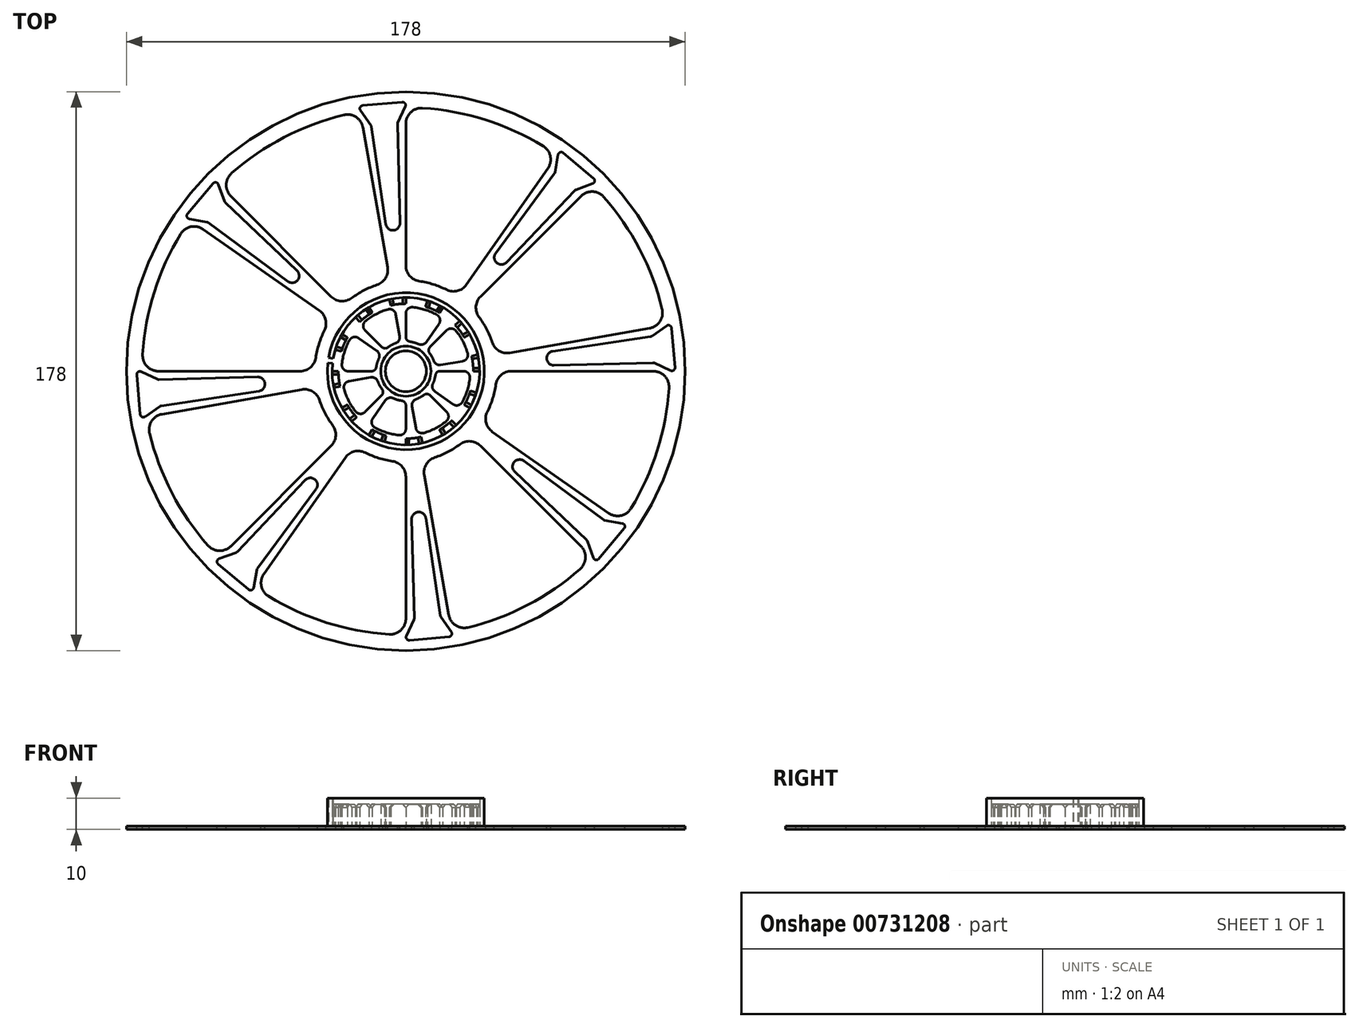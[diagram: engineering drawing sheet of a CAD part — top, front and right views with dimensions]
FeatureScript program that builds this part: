
annotation { "Feature Type Name" : "Feature", "Feature Type Description" : "" }
export const myFeature = defineFeature(function(context is Context, id is Id, definition is map)
    precondition{}
    {
        {
            var Q0;
            Q0=qCreatedBy(makeId("Top.planeOp"),FACE);
            var sketch = newSketch(context, id + "F0", { "sketchPlane" : qUnion([Q0])});
            skCircle(sketch, "E0", {"center": v(0, 0) * mm, "radius": 89 * mm});
            skCircle(sketch, "E1", {"center": v(0, 0) * mm, "radius": 6.5 * mm});
            skSolve(sketch);
        }
        {
            var Q0;
            Q0 = qSketchRegion(id + "F0", true);
            extrude(context, id + "F1", {"entities" : qUnion([Q0]), "depth" : 1 * mm, "offsetDistance" : 25 * mm});
        }
        {
            var Q0;
            Q0=makeQuery(id+"F1.opExtrude","CAP_FACE",FACE,{"disambiguationData":[OSD([sQuery(id+"F0.wireOp",EDGE,"E0"),sQuery(id+"F0.wireOp",EDGE,"E1")])],"isStart":false});
            var sketch = newSketch(context, id + "F2", { "sketchPlane" : qUnion([Q0])});
            skCircle(sketch, "E2", {"center": v(0, 0) * mm, "radius": 25 * mm});
            skCircle(sketch, "E3.0", {"center": v(0, 0) * mm, "radius": 23.5 * mm});
            skSolve(sketch);
        }
        {
            var Q0;
            Q0 = qSketchRegion(id + "F2", true);
            extrude(context, id + "F3", {"entities" : qUnion([Q0]), "operationType" : NewBodyOperationType.ADD, "depth" : 9 * mm, "offsetDistance" : 25 * mm});
        }
        {
            var Q0;
            {var subQ0=sQuery(id+"F0.wireOp",EDGE,"E0");Q0=makeQuery(id+"F3.boolean.opBoolean","SPLIT",FACE,{"disambiguationData":[TD([makeQuery(id+"F1.opExtrude","SWEPT_FACE",FACE,{"disambiguationData":[OSD([subQ0])]})])],"derivedFrom":makeQuery(id+"F1.opExtrude","CAP_FACE",FACE,{"disambiguationData":[OSD([subQ0,sQuery(id+"F0.wireOp",EDGE,"E1")])],"isStart":false})});}
            var sketch = newSketch(context, id + "F4", { "sketchPlane" : qUnion([Q0])});
            skLineSegment(sketch, "E4", {"start": v(-78.84, 0) * mm, "end": v(-33.63, 0) * mm});
            skLineSegment(sketch, "E5", {"start": v(-64.58, 45.22) * mm, "end": v(-27.55, 19.29) * mm});
            skPoint(sketch, "E6.center", {"position": v(0, 0) * mm});
            skArc(sketch, "E7", {"start": v(-28.68, 4.26) * mm, "mid": v(-27.66, 8.72) * mm, "end": v(-25.94, 12.96) * mm});
            skArc(sketch, "E8", {"start": v(-83.83, 5.32) * mm, "mid": v(-80.11, 25.26) * mm, "end": v(-71.72, 43.73) * mm});
            skPoint(sketch, "E9.visualSharp", {"position": v(-68.8, 48.18) * mm});
            skArc(sketch, "E9.filletArc", {"start": v(-64.58, 45.22) * mm, "mid": v(-68.47, 46.02) * mm, "end": v(-71.72, 43.73) * mm});
            skPoint(sketch, "E10.visualSharp", {"position": v(-84, 0) * mm});
            skArc(sketch, "E10.filletArc", {"start": v(-83.83, 5.32) * mm, "mid": v(-82.49, 1.58) * mm, "end": v(-78.84, 0) * mm});
            skPoint(sketch, "E11.visualSharp", {"position": v(-23.76, 16.63) * mm});
            skArc(sketch, "E11.filletArc", {"start": v(-25.94, 12.96) * mm, "mid": v(-25.57, 16.42) * mm, "end": v(-27.55, 19.29) * mm});
            skPoint(sketch, "E12.visualSharp", {"position": v(-29, 0) * mm});
            skArc(sketch, "E12.filletArc", {"start": v(-33.63, 0) * mm, "mid": v(-30.37, 1.21) * mm, "end": v(-28.68, 4.26) * mm});
            skArc(sketch, "E13.1.0", {"start": v(-63.04, -55.52) * mm, "mid": v(-74.5, -38.79) * mm, "end": v(-81.63, -19.8) * mm});
            skArc(sketch, "E13.1.1", {"start": v(-23.3, -17.27) * mm, "mid": v(-25.72, -13.4) * mm, "end": v(-27.5, -9.18) * mm});
            skPoint(sketch, "E13.1.2", {"position": v(-28.56, -5.04) * mm});
            skPoint(sketch, "E13.1.3", {"position": v(-59.4, -59.4) * mm});
            skPoint(sketch, "E13.1.4", {"position": v(-20.5, -20.5) * mm});
            skLineSegment(sketch, "E13.1.5", {"start": v(-77.64, -13.7) * mm, "end": v(-33.12, -5.84) * mm});
            skPoint(sketch, "E13.1.6", {"position": v(-82.72, -14.59) * mm});
            skLineSegment(sketch, "E13.1.7", {"start": v(-55.75, -55.75) * mm, "end": v(-23.78, -23.78) * mm});
            skArc(sketch, "E13.1.8", {"start": v(-63.04, -55.52) * mm, "mid": v(-59.44, -57.21) * mm, "end": v(-55.75, -55.75) * mm});
            skArc(sketch, "E13.1.9", {"start": v(-23.78, -23.78) * mm, "mid": v(-22.33, -20.61) * mm, "end": v(-23.3, -17.27) * mm});
            skArc(sketch, "E13.1.10", {"start": v(-27.5, -9.18) * mm, "mid": v(-29.7, -6.47) * mm, "end": v(-33.12, -5.84) * mm});
            skArc(sketch, "E13.1.11", {"start": v(-77.64, -13.7) * mm, "mid": v(-80.96, -15.88) * mm, "end": v(-81.63, -19.8) * mm});
            skArc(sketch, "E13.2.0", {"start": v(-5.32, -83.83) * mm, "mid": v(-25.26, -80.11) * mm, "end": v(-43.73, -71.72) * mm});
            skArc(sketch, "E13.2.1", {"start": v(-4.26, -28.68) * mm, "mid": v(-8.72, -27.66) * mm, "end": v(-12.96, -25.94) * mm});
            skPoint(sketch, "E13.2.2", {"position": v(-16.63, -23.76) * mm});
            skPoint(sketch, "E13.2.3", {"position": v(0, -84) * mm});
            skPoint(sketch, "E13.2.4", {"position": v(0, -29) * mm});
            skLineSegment(sketch, "E13.2.5", {"start": v(-45.22, -64.58) * mm, "end": v(-19.29, -27.55) * mm});
            skPoint(sketch, "E13.2.6", {"position": v(-48.18, -68.8) * mm});
            skLineSegment(sketch, "E13.2.7", {"start": v(0, -78.84) * mm, "end": v(0, -33.63) * mm});
            skArc(sketch, "E13.2.8", {"start": v(-5.32, -83.83) * mm, "mid": v(-1.58, -82.49) * mm, "end": v(0, -78.84) * mm});
            skArc(sketch, "E13.2.9", {"start": v(0, -33.63) * mm, "mid": v(-1.21, -30.37) * mm, "end": v(-4.26, -28.68) * mm});
            skArc(sketch, "E13.2.10", {"start": v(-12.96, -25.94) * mm, "mid": v(-16.42, -25.57) * mm, "end": v(-19.29, -27.55) * mm});
            skArc(sketch, "E13.2.11", {"start": v(-45.22, -64.58) * mm, "mid": v(-46.02, -68.47) * mm, "end": v(-43.73, -71.72) * mm});
            skArc(sketch, "E13.3.0", {"start": v(55.52, -63.04) * mm, "mid": v(38.79, -74.5) * mm, "end": v(19.8, -81.63) * mm});
            skArc(sketch, "E13.3.1", {"start": v(17.27, -23.3) * mm, "mid": v(13.4, -25.72) * mm, "end": v(9.18, -27.5) * mm});
            skPoint(sketch, "E13.3.2", {"position": v(5.04, -28.56) * mm});
            skPoint(sketch, "E13.3.3", {"position": v(59.4, -59.4) * mm});
            skPoint(sketch, "E13.3.4", {"position": v(20.5, -20.5) * mm});
            skLineSegment(sketch, "E13.3.5", {"start": v(13.7, -77.64) * mm, "end": v(5.84, -33.12) * mm});
            skPoint(sketch, "E13.3.6", {"position": v(14.59, -82.72) * mm});
            skLineSegment(sketch, "E13.3.7", {"start": v(55.75, -55.75) * mm, "end": v(23.78, -23.78) * mm});
            skArc(sketch, "E13.3.8", {"start": v(55.52, -63.04) * mm, "mid": v(57.21, -59.44) * mm, "end": v(55.75, -55.75) * mm});
            skArc(sketch, "E13.3.9", {"start": v(23.78, -23.78) * mm, "mid": v(20.61, -22.33) * mm, "end": v(17.27, -23.3) * mm});
            skArc(sketch, "E13.3.10", {"start": v(9.18, -27.5) * mm, "mid": v(6.47, -29.7) * mm, "end": v(5.84, -33.12) * mm});
            skArc(sketch, "E13.3.11", {"start": v(13.7, -77.64) * mm, "mid": v(15.88, -80.96) * mm, "end": v(19.8, -81.63) * mm});
            skArc(sketch, "E13.4.0", {"start": v(83.83, -5.32) * mm, "mid": v(80.11, -25.26) * mm, "end": v(71.72, -43.73) * mm});
            skArc(sketch, "E13.4.1", {"start": v(28.68, -4.26) * mm, "mid": v(27.66, -8.72) * mm, "end": v(25.94, -12.96) * mm});
            skPoint(sketch, "E13.4.2", {"position": v(23.76, -16.63) * mm});
            skPoint(sketch, "E13.4.3", {"position": v(84, 0) * mm});
            skPoint(sketch, "E13.4.4", {"position": v(29, 0) * mm});
            skLineSegment(sketch, "E13.4.5", {"start": v(64.58, -45.22) * mm, "end": v(27.55, -19.29) * mm});
            skPoint(sketch, "E13.4.6", {"position": v(68.8, -48.18) * mm});
            skLineSegment(sketch, "E13.4.7", {"start": v(78.84, 0) * mm, "end": v(33.63, 0) * mm});
            skArc(sketch, "E13.4.8", {"start": v(83.83, -5.32) * mm, "mid": v(82.49, -1.58) * mm, "end": v(78.84, 0) * mm});
            skArc(sketch, "E13.4.9", {"start": v(33.63, 0) * mm, "mid": v(30.37, -1.21) * mm, "end": v(28.68, -4.26) * mm});
            skArc(sketch, "E13.4.10", {"start": v(25.94, -12.96) * mm, "mid": v(25.57, -16.42) * mm, "end": v(27.55, -19.29) * mm});
            skArc(sketch, "E13.4.11", {"start": v(64.58, -45.22) * mm, "mid": v(68.47, -46.02) * mm, "end": v(71.72, -43.73) * mm});
            skArc(sketch, "E13.5.0", {"start": v(63.04, 55.52) * mm, "mid": v(74.5, 38.79) * mm, "end": v(81.63, 19.8) * mm});
            skArc(sketch, "E13.5.1", {"start": v(23.3, 17.27) * mm, "mid": v(25.72, 13.4) * mm, "end": v(27.5, 9.18) * mm});
            skPoint(sketch, "E13.5.2", {"position": v(28.56, 5.04) * mm});
            skPoint(sketch, "E13.5.3", {"position": v(59.4, 59.4) * mm});
            skPoint(sketch, "E13.5.4", {"position": v(20.5, 20.5) * mm});
            skLineSegment(sketch, "E13.5.5", {"start": v(77.64, 13.7) * mm, "end": v(33.12, 5.84) * mm});
            skPoint(sketch, "E13.5.6", {"position": v(82.72, 14.59) * mm});
            skLineSegment(sketch, "E13.5.7", {"start": v(55.75, 55.75) * mm, "end": v(23.78, 23.78) * mm});
            skArc(sketch, "E13.5.8", {"start": v(63.04, 55.52) * mm, "mid": v(59.44, 57.21) * mm, "end": v(55.75, 55.75) * mm});
            skArc(sketch, "E13.5.9", {"start": v(23.78, 23.78) * mm, "mid": v(22.33, 20.61) * mm, "end": v(23.3, 17.27) * mm});
            skArc(sketch, "E13.5.10", {"start": v(27.5, 9.18) * mm, "mid": v(29.7, 6.47) * mm, "end": v(33.12, 5.84) * mm});
            skArc(sketch, "E13.5.11", {"start": v(77.64, 13.7) * mm, "mid": v(80.96, 15.88) * mm, "end": v(81.63, 19.8) * mm});
            skArc(sketch, "E13.6.0", {"start": v(5.32, 83.83) * mm, "mid": v(25.26, 80.11) * mm, "end": v(43.73, 71.72) * mm});
            skArc(sketch, "E13.6.1", {"start": v(4.26, 28.68) * mm, "mid": v(8.72, 27.66) * mm, "end": v(12.96, 25.94) * mm});
            skPoint(sketch, "E13.6.2", {"position": v(16.63, 23.76) * mm});
            skPoint(sketch, "E13.6.3", {"position": v(0, 84) * mm});
            skPoint(sketch, "E13.6.4", {"position": v(0, 29) * mm});
            skLineSegment(sketch, "E13.6.5", {"start": v(45.22, 64.58) * mm, "end": v(19.29, 27.55) * mm});
            skPoint(sketch, "E13.6.6", {"position": v(48.18, 68.8) * mm});
            skLineSegment(sketch, "E13.6.7", {"start": v(0, 78.84) * mm, "end": v(0, 33.63) * mm});
            skArc(sketch, "E13.6.8", {"start": v(5.32, 83.83) * mm, "mid": v(1.58, 82.49) * mm, "end": v(0, 78.84) * mm});
            skArc(sketch, "E13.6.9", {"start": v(0, 33.63) * mm, "mid": v(1.21, 30.37) * mm, "end": v(4.26, 28.68) * mm});
            skArc(sketch, "E13.6.10", {"start": v(12.96, 25.94) * mm, "mid": v(16.42, 25.57) * mm, "end": v(19.29, 27.55) * mm});
            skArc(sketch, "E13.6.11", {"start": v(45.22, 64.58) * mm, "mid": v(46.02, 68.47) * mm, "end": v(43.73, 71.72) * mm});
            skArc(sketch, "E13.7.0", {"start": v(-55.52, 63.04) * mm, "mid": v(-38.79, 74.5) * mm, "end": v(-19.8, 81.63) * mm});
            skArc(sketch, "E13.7.1", {"start": v(-17.27, 23.3) * mm, "mid": v(-13.4, 25.72) * mm, "end": v(-9.18, 27.5) * mm});
            skPoint(sketch, "E13.7.2", {"position": v(-5.04, 28.56) * mm});
            skPoint(sketch, "E13.7.3", {"position": v(-59.4, 59.4) * mm});
            skPoint(sketch, "E13.7.4", {"position": v(-20.5, 20.5) * mm});
            skLineSegment(sketch, "E13.7.5", {"start": v(-13.7, 77.64) * mm, "end": v(-5.84, 33.12) * mm});
            skPoint(sketch, "E13.7.6", {"position": v(-14.59, 82.72) * mm});
            skLineSegment(sketch, "E13.7.7", {"start": v(-55.75, 55.75) * mm, "end": v(-23.78, 23.78) * mm});
            skArc(sketch, "E13.7.8", {"start": v(-55.52, 63.04) * mm, "mid": v(-57.21, 59.44) * mm, "end": v(-55.75, 55.75) * mm});
            skArc(sketch, "E13.7.9", {"start": v(-23.78, 23.78) * mm, "mid": v(-20.61, 22.33) * mm, "end": v(-17.27, 23.3) * mm});
            skArc(sketch, "E13.7.10", {"start": v(-9.18, 27.5) * mm, "mid": v(-6.47, 29.7) * mm, "end": v(-5.84, 33.12) * mm});
            skArc(sketch, "E13.7.11", {"start": v(-13.7, 77.64) * mm, "mid": v(-15.88, 80.96) * mm, "end": v(-19.8, 81.63) * mm});
            skLineSegment(sketch, "E14", {"start": v(-62.9, 47.32) * mm, "end": v(-37.6, 28.6) * mm});
            skLineSegment(sketch, "E15", {"start": v(-34.7, 32.07) * mm, "end": v(-57.52, 53.73) * mm});
            skLineSegment(sketch, "E16", {"start": v(-57.78, 54.12) * mm, "end": v(-59.73, 59.5) * mm});
            skLineSegment(sketch, "E17", {"start": v(-68.96, 48.5) * mm, "end": v(-63.33, 47.5) * mm});
            skArc(sketch, "E18", {"start": v(-37.6, 28.6) * mm, "mid": v(-34.52, 28.96) * mm, "end": v(-34.7, 32.07) * mm});
            skLineSegment(sketch, "E19", {"start": v(-57.7, 53.9) * mm, "end": v(-63.1, 47.46) * mm, "construction": true});
            skPoint(sketch, "E20", {"position": v(-60.4, 50.68) * mm});
            skLineSegment(sketch, "E21", {"start": v(-60.4, 50.68) * mm, "end": v(-36.25, 30.42) * mm, "construction": true});
            skLineSegment(sketch, "E22", {"start": v(-61.44, 59.8) * mm, "end": v(-69.56, 50.12) * mm});
            skPoint(sketch, "E23", {"position": v(-65.5, 54.96) * mm});
            skPoint(sketch, "E24", {"position": v(-68.18, 57.2) * mm});
            skLineSegment(sketch, "E25", {"start": v(-57.27, 70.2) * mm, "end": v(-81.87, 40.9) * mm, "construction": true});
            skPoint(sketch, "E26.visualSharp", {"position": v(-70.67, 48.8) * mm});
            skArc(sketch, "E26.filletArc", {"start": v(-69.56, 50.12) * mm, "mid": v(-69.73, 49.14) * mm, "end": v(-68.96, 48.5) * mm});
            skPoint(sketch, "E27.visualSharp", {"position": v(-60.33, 61.12) * mm});
            skArc(sketch, "E27.filletArc", {"start": v(-59.73, 59.5) * mm, "mid": v(-60.5, 60.14) * mm, "end": v(-61.44, 59.8) * mm});
            skPoint(sketch, "E28.visualSharp", {"position": v(-57.7, 53.9) * mm});
            skArc(sketch, "E28.filletArc", {"start": v(-57.78, 54.12) * mm, "mid": v(-57.67, 53.91) * mm, "end": v(-57.52, 53.73) * mm});
            skPoint(sketch, "E29.visualSharp", {"position": v(-63.1, 47.46) * mm});
            skArc(sketch, "E29.filletArc", {"start": v(-62.9, 47.32) * mm, "mid": v(-63.1, 47.43) * mm, "end": v(-63.33, 47.5) * mm});
            skArc(sketch, "E30", {"start": v(-64.58, 45.22) * mm, "mid": v(-62.55, 48) * mm, "end": v(-60.4, 50.68) * mm, "construction": true});
            skArc(sketch, "E31.1.0", {"start": v(-46.81, -6.37) * mm, "mid": v(-44.88, -3.93) * mm, "end": v(-47.2, -1.86) * mm});
            skLineSegment(sketch, "E31.1.1", {"start": v(-77.94, -11.02) * mm, "end": v(-46.81, -6.37) * mm});
            skLineSegment(sketch, "E31.1.2", {"start": v(-47.2, -1.86) * mm, "end": v(-78.67, -2.68) * mm});
            skLineSegment(sketch, "E31.1.3", {"start": v(-79.12, -2.59) * mm, "end": v(-84.3, -0.17) * mm});
            skLineSegment(sketch, "E31.1.4", {"start": v(-85.72, -1.16) * mm, "end": v(-84.62, -13.74) * mm});
            skLineSegment(sketch, "E31.1.5", {"start": v(-83.05, -14.47) * mm, "end": v(-78.37, -11.2) * mm});
            skArc(sketch, "E31.1.6", {"start": v(-84.62, -13.74) * mm, "mid": v(-84.05, -14.56) * mm, "end": v(-83.05, -14.47) * mm});
            skArc(sketch, "E31.1.7", {"start": v(-84.3, -0.17) * mm, "mid": v(-85.3, -0.26) * mm, "end": v(-85.72, -1.16) * mm});
            skArc(sketch, "E31.1.8", {"start": v(-79.12, -2.59) * mm, "mid": v(-78.9, -2.66) * mm, "end": v(-78.67, -2.68) * mm});
            skArc(sketch, "E31.1.9", {"start": v(-77.94, -11.02) * mm, "mid": v(-78.17, -11.08) * mm, "end": v(-78.37, -11.2) * mm});
            skArc(sketch, "E31.2.0", {"start": v(-28.6, -37.6) * mm, "mid": v(-28.96, -34.52) * mm, "end": v(-32.07, -34.7) * mm});
            skLineSegment(sketch, "E31.2.1", {"start": v(-47.32, -62.9) * mm, "end": v(-28.6, -37.6) * mm});
            skLineSegment(sketch, "E31.2.2", {"start": v(-32.07, -34.7) * mm, "end": v(-53.73, -57.52) * mm});
            skLineSegment(sketch, "E31.2.3", {"start": v(-54.12, -57.78) * mm, "end": v(-59.5, -59.73) * mm});
            skLineSegment(sketch, "E31.2.4", {"start": v(-59.8, -61.44) * mm, "end": v(-50.12, -69.56) * mm});
            skLineSegment(sketch, "E31.2.5", {"start": v(-48.5, -68.96) * mm, "end": v(-47.5, -63.33) * mm});
            skArc(sketch, "E31.2.6", {"start": v(-50.12, -69.56) * mm, "mid": v(-49.14, -69.73) * mm, "end": v(-48.5, -68.96) * mm});
            skArc(sketch, "E31.2.7", {"start": v(-59.5, -59.73) * mm, "mid": v(-60.14, -60.5) * mm, "end": v(-59.8, -61.44) * mm});
            skArc(sketch, "E31.2.8", {"start": v(-54.12, -57.78) * mm, "mid": v(-53.91, -57.67) * mm, "end": v(-53.73, -57.52) * mm});
            skArc(sketch, "E31.2.9", {"start": v(-47.32, -62.9) * mm, "mid": v(-47.43, -63.1) * mm, "end": v(-47.5, -63.33) * mm});
            skArc(sketch, "E31.3.0", {"start": v(6.37, -46.81) * mm, "mid": v(3.93, -44.88) * mm, "end": v(1.86, -47.2) * mm});
            skLineSegment(sketch, "E31.3.1", {"start": v(11.02, -77.94) * mm, "end": v(6.37, -46.81) * mm});
            skLineSegment(sketch, "E31.3.2", {"start": v(1.86, -47.2) * mm, "end": v(2.68, -78.67) * mm});
            skLineSegment(sketch, "E31.3.3", {"start": v(2.59, -79.12) * mm, "end": v(0.17, -84.3) * mm});
            skLineSegment(sketch, "E31.3.4", {"start": v(1.16, -85.72) * mm, "end": v(13.74, -84.62) * mm});
            skLineSegment(sketch, "E31.3.5", {"start": v(14.47, -83.05) * mm, "end": v(11.2, -78.37) * mm});
            skArc(sketch, "E31.3.6", {"start": v(13.74, -84.62) * mm, "mid": v(14.56, -84.05) * mm, "end": v(14.47, -83.05) * mm});
            skArc(sketch, "E31.3.7", {"start": v(0.17, -84.3) * mm, "mid": v(0.26, -85.3) * mm, "end": v(1.16, -85.72) * mm});
            skArc(sketch, "E31.3.8", {"start": v(2.59, -79.12) * mm, "mid": v(2.66, -78.9) * mm, "end": v(2.68, -78.67) * mm});
            skArc(sketch, "E31.3.9", {"start": v(11.02, -77.94) * mm, "mid": v(11.08, -78.17) * mm, "end": v(11.2, -78.37) * mm});
            skArc(sketch, "E31.4.0", {"start": v(37.6, -28.6) * mm, "mid": v(34.52, -28.96) * mm, "end": v(34.7, -32.07) * mm});
            skLineSegment(sketch, "E31.4.1", {"start": v(62.9, -47.32) * mm, "end": v(37.6, -28.6) * mm});
            skLineSegment(sketch, "E31.4.2", {"start": v(34.7, -32.07) * mm, "end": v(57.52, -53.73) * mm});
            skLineSegment(sketch, "E31.4.3", {"start": v(57.78, -54.12) * mm, "end": v(59.73, -59.5) * mm});
            skLineSegment(sketch, "E31.4.4", {"start": v(61.44, -59.8) * mm, "end": v(69.56, -50.12) * mm});
            skLineSegment(sketch, "E31.4.5", {"start": v(68.96, -48.5) * mm, "end": v(63.33, -47.5) * mm});
            skArc(sketch, "E31.4.6", {"start": v(69.56, -50.12) * mm, "mid": v(69.73, -49.14) * mm, "end": v(68.96, -48.5) * mm});
            skArc(sketch, "E31.4.7", {"start": v(59.73, -59.5) * mm, "mid": v(60.5, -60.14) * mm, "end": v(61.44, -59.8) * mm});
            skArc(sketch, "E31.4.8", {"start": v(57.78, -54.12) * mm, "mid": v(57.67, -53.91) * mm, "end": v(57.52, -53.73) * mm});
            skArc(sketch, "E31.4.9", {"start": v(62.9, -47.32) * mm, "mid": v(63.1, -47.43) * mm, "end": v(63.33, -47.5) * mm});
            skArc(sketch, "E31.5.0", {"start": v(46.81, 6.37) * mm, "mid": v(44.88, 3.93) * mm, "end": v(47.2, 1.86) * mm});
            skLineSegment(sketch, "E31.5.1", {"start": v(77.94, 11.02) * mm, "end": v(46.81, 6.37) * mm});
            skLineSegment(sketch, "E31.5.2", {"start": v(47.2, 1.86) * mm, "end": v(78.67, 2.68) * mm});
            skLineSegment(sketch, "E31.5.3", {"start": v(79.12, 2.59) * mm, "end": v(84.3, 0.17) * mm});
            skLineSegment(sketch, "E31.5.4", {"start": v(85.72, 1.16) * mm, "end": v(84.62, 13.74) * mm});
            skLineSegment(sketch, "E31.5.5", {"start": v(83.05, 14.47) * mm, "end": v(78.37, 11.2) * mm});
            skArc(sketch, "E31.5.6", {"start": v(84.62, 13.74) * mm, "mid": v(84.05, 14.56) * mm, "end": v(83.05, 14.47) * mm});
            skArc(sketch, "E31.5.7", {"start": v(84.3, 0.17) * mm, "mid": v(85.3, 0.26) * mm, "end": v(85.72, 1.16) * mm});
            skArc(sketch, "E31.5.8", {"start": v(79.12, 2.59) * mm, "mid": v(78.9, 2.66) * mm, "end": v(78.67, 2.68) * mm});
            skArc(sketch, "E31.5.9", {"start": v(77.94, 11.02) * mm, "mid": v(78.17, 11.08) * mm, "end": v(78.37, 11.2) * mm});
            skArc(sketch, "E31.6.0", {"start": v(28.6, 37.6) * mm, "mid": v(28.96, 34.52) * mm, "end": v(32.07, 34.7) * mm});
            skLineSegment(sketch, "E31.6.1", {"start": v(47.32, 62.9) * mm, "end": v(28.6, 37.6) * mm});
            skLineSegment(sketch, "E31.6.2", {"start": v(32.07, 34.7) * mm, "end": v(53.73, 57.52) * mm});
            skLineSegment(sketch, "E31.6.3", {"start": v(54.12, 57.78) * mm, "end": v(59.5, 59.73) * mm});
            skLineSegment(sketch, "E31.6.4", {"start": v(59.8, 61.44) * mm, "end": v(50.12, 69.56) * mm});
            skLineSegment(sketch, "E31.6.5", {"start": v(48.5, 68.96) * mm, "end": v(47.5, 63.33) * mm});
            skArc(sketch, "E31.6.6", {"start": v(50.12, 69.56) * mm, "mid": v(49.14, 69.73) * mm, "end": v(48.5, 68.96) * mm});
            skArc(sketch, "E31.6.7", {"start": v(59.5, 59.73) * mm, "mid": v(60.14, 60.5) * mm, "end": v(59.8, 61.44) * mm});
            skArc(sketch, "E31.6.8", {"start": v(54.12, 57.78) * mm, "mid": v(53.91, 57.67) * mm, "end": v(53.73, 57.52) * mm});
            skArc(sketch, "E31.6.9", {"start": v(47.32, 62.9) * mm, "mid": v(47.43, 63.1) * mm, "end": v(47.5, 63.33) * mm});
            skArc(sketch, "E31.7.0", {"start": v(-6.37, 46.81) * mm, "mid": v(-3.93, 44.88) * mm, "end": v(-1.86, 47.2) * mm});
            skLineSegment(sketch, "E31.7.1", {"start": v(-11.02, 77.94) * mm, "end": v(-6.37, 46.81) * mm});
            skLineSegment(sketch, "E31.7.2", {"start": v(-1.86, 47.2) * mm, "end": v(-2.68, 78.67) * mm});
            skLineSegment(sketch, "E31.7.3", {"start": v(-2.59, 79.12) * mm, "end": v(-0.17, 84.3) * mm});
            skLineSegment(sketch, "E31.7.4", {"start": v(-1.16, 85.72) * mm, "end": v(-13.74, 84.62) * mm});
            skLineSegment(sketch, "E31.7.5", {"start": v(-14.47, 83.05) * mm, "end": v(-11.2, 78.37) * mm});
            skArc(sketch, "E31.7.6", {"start": v(-13.74, 84.62) * mm, "mid": v(-14.56, 84.05) * mm, "end": v(-14.47, 83.05) * mm});
            skArc(sketch, "E31.7.7", {"start": v(-0.17, 84.3) * mm, "mid": v(-0.26, 85.3) * mm, "end": v(-1.16, 85.72) * mm});
            skArc(sketch, "E31.7.8", {"start": v(-2.59, 79.12) * mm, "mid": v(-2.66, 78.9) * mm, "end": v(-2.68, 78.67) * mm});
            skArc(sketch, "E31.7.9", {"start": v(-11.02, 77.94) * mm, "mid": v(-11.08, 78.17) * mm, "end": v(-11.2, 78.37) * mm});
            skLineSegment(sketch, "E32", {"start": v(-18.4, 0) * mm, "end": v(-10.9, 0) * mm});
            skLineSegment(sketch, "E33", {"start": v(-9.28, 6.5) * mm, "end": v(-15.07, 10.55) * mm});
            skArc(sketch, "E34", {"start": v(-9.41, 1.3) * mm, "mid": v(-9.11, 2.68) * mm, "end": v(-8.61, 4.01) * mm});
            skArc(sketch, "E35", {"start": v(-20.38, 2.22) * mm, "mid": v(-19.55, 6.16) * mm, "end": v(-17.97, 9.87) * mm});
            skPoint(sketch, "E36.visualSharp", {"position": v(-16.8, 11.76) * mm});
            skArc(sketch, "E36.filletArc", {"start": v(-15.07, 10.55) * mm, "mid": v(-16.67, 10.86) * mm, "end": v(-17.97, 9.87) * mm});
            skPoint(sketch, "E37.visualSharp", {"position": v(-20.5, 0) * mm});
            skArc(sketch, "E37.filletArc", {"start": v(-20.38, 2.22) * mm, "mid": v(-19.88, 0.66) * mm, "end": v(-18.4, 0) * mm});
            skPoint(sketch, "E38.visualSharp", {"position": v(-9.5, 0) * mm});
            skArc(sketch, "E38.filletArc", {"start": v(-10.9, 0) * mm, "mid": v(-9.91, 0.37) * mm, "end": v(-9.41, 1.3) * mm});
            skPoint(sketch, "E39.visualSharp", {"position": v(-7.78, 5.45) * mm});
            skArc(sketch, "E39.filletArc", {"start": v(-8.61, 4.01) * mm, "mid": v(-8.5, 5.38) * mm, "end": v(-9.28, 6.5) * mm});
            skLineSegment(sketch, "E40.1.0", {"start": v(-13, -13) * mm, "end": v(-7.7, -7.7) * mm});
            skArc(sketch, "E40.1.1", {"start": v(-7.57, -5.74) * mm, "mid": v(-8.34, -4.55) * mm, "end": v(-8.93, -3.25) * mm});
            skPoint(sketch, "E40.1.2", {"position": v(-20.19, -3.56) * mm});
            skPoint(sketch, "E40.1.3", {"position": v(-9.36, -1.65) * mm});
            skPoint(sketch, "E40.1.4", {"position": v(-6.72, -6.72) * mm});
            skLineSegment(sketch, "E40.1.5", {"start": v(-11.15, -1.97) * mm, "end": v(-18.11, -3.2) * mm});
            skArc(sketch, "E40.1.6", {"start": v(-8.93, -3.25) * mm, "mid": v(-9.8, -2.2) * mm, "end": v(-11.15, -1.97) * mm});
            skArc(sketch, "E40.1.7", {"start": v(-18.11, -3.2) * mm, "mid": v(-19.46, -4.1) * mm, "end": v(-19.69, -5.72) * mm});
            skArc(sketch, "E40.1.8", {"start": v(-7.7, -7.7) * mm, "mid": v(-7.27, -6.75) * mm, "end": v(-7.57, -5.74) * mm});
            skArc(sketch, "E40.1.9", {"start": v(-15.98, -12.84) * mm, "mid": v(-14.53, -13.59) * mm, "end": v(-13, -13) * mm});
            skArc(sketch, "E40.1.10", {"start": v(-15.98, -12.84) * mm, "mid": v(-18.18, -9.47) * mm, "end": v(-19.69, -5.72) * mm});
            skLineSegment(sketch, "E40.2.0", {"start": v(0, -18.4) * mm, "end": v(0, -10.9) * mm});
            skArc(sketch, "E40.2.1", {"start": v(-1.3, -9.41) * mm, "mid": v(-2.68, -9.11) * mm, "end": v(-4.01, -8.61) * mm});
            skPoint(sketch, "E40.2.2", {"position": v(-11.76, -16.8) * mm});
            skPoint(sketch, "E40.2.3", {"position": v(-5.45, -7.78) * mm});
            skPoint(sketch, "E40.2.4", {"position": v(0, -9.5) * mm});
            skLineSegment(sketch, "E40.2.5", {"start": v(-6.5, -9.28) * mm, "end": v(-10.55, -15.07) * mm});
            skArc(sketch, "E40.2.6", {"start": v(-4.01, -8.61) * mm, "mid": v(-5.38, -8.5) * mm, "end": v(-6.5, -9.28) * mm});
            skArc(sketch, "E40.2.7", {"start": v(-10.55, -15.07) * mm, "mid": v(-10.86, -16.67) * mm, "end": v(-9.87, -17.97) * mm});
            skArc(sketch, "E40.2.8", {"start": v(0, -10.9) * mm, "mid": v(-0.37, -9.91) * mm, "end": v(-1.3, -9.41) * mm});
            skArc(sketch, "E40.2.9", {"start": v(-2.22, -20.38) * mm, "mid": v(-0.66, -19.88) * mm, "end": v(0, -18.4) * mm});
            skArc(sketch, "E40.2.10", {"start": v(-2.22, -20.38) * mm, "mid": v(-6.16, -19.55) * mm, "end": v(-9.87, -17.97) * mm});
            skLineSegment(sketch, "E40.3.0", {"start": v(13, -13) * mm, "end": v(7.7, -7.7) * mm});
            skArc(sketch, "E40.3.1", {"start": v(5.74, -7.57) * mm, "mid": v(4.55, -8.34) * mm, "end": v(3.25, -8.93) * mm});
            skPoint(sketch, "E40.3.2", {"position": v(3.56, -20.19) * mm});
            skPoint(sketch, "E40.3.3", {"position": v(1.65, -9.36) * mm});
            skPoint(sketch, "E40.3.4", {"position": v(6.72, -6.72) * mm});
            skLineSegment(sketch, "E40.3.5", {"start": v(1.97, -11.15) * mm, "end": v(3.2, -18.11) * mm});
            skArc(sketch, "E40.3.6", {"start": v(3.25, -8.93) * mm, "mid": v(2.2, -9.8) * mm, "end": v(1.97, -11.15) * mm});
            skArc(sketch, "E40.3.7", {"start": v(3.2, -18.11) * mm, "mid": v(4.1, -19.46) * mm, "end": v(5.72, -19.69) * mm});
            skArc(sketch, "E40.3.8", {"start": v(7.7, -7.7) * mm, "mid": v(6.75, -7.27) * mm, "end": v(5.74, -7.57) * mm});
            skArc(sketch, "E40.3.9", {"start": v(12.84, -15.98) * mm, "mid": v(13.59, -14.53) * mm, "end": v(13, -13) * mm});
            skArc(sketch, "E40.3.10", {"start": v(12.84, -15.98) * mm, "mid": v(9.47, -18.18) * mm, "end": v(5.72, -19.69) * mm});
            skLineSegment(sketch, "E40.4.0", {"start": v(18.4, 0) * mm, "end": v(10.9, 0) * mm});
            skArc(sketch, "E40.4.1", {"start": v(9.41, -1.3) * mm, "mid": v(9.11, -2.68) * mm, "end": v(8.61, -4.01) * mm});
            skPoint(sketch, "E40.4.2", {"position": v(16.8, -11.76) * mm});
            skPoint(sketch, "E40.4.3", {"position": v(7.78, -5.45) * mm});
            skPoint(sketch, "E40.4.4", {"position": v(9.5, 0) * mm});
            skLineSegment(sketch, "E40.4.5", {"start": v(9.28, -6.5) * mm, "end": v(15.07, -10.55) * mm});
            skArc(sketch, "E40.4.6", {"start": v(8.61, -4.01) * mm, "mid": v(8.5, -5.38) * mm, "end": v(9.28, -6.5) * mm});
            skArc(sketch, "E40.4.7", {"start": v(15.07, -10.55) * mm, "mid": v(16.67, -10.86) * mm, "end": v(17.97, -9.87) * mm});
            skArc(sketch, "E40.4.8", {"start": v(10.9, 0) * mm, "mid": v(9.91, -0.37) * mm, "end": v(9.41, -1.3) * mm});
            skArc(sketch, "E40.4.9", {"start": v(20.38, -2.22) * mm, "mid": v(19.88, -0.66) * mm, "end": v(18.4, 0) * mm});
            skArc(sketch, "E40.4.10", {"start": v(20.38, -2.22) * mm, "mid": v(19.55, -6.16) * mm, "end": v(17.97, -9.87) * mm});
            skLineSegment(sketch, "E40.5.0", {"start": v(13, 13) * mm, "end": v(7.7, 7.7) * mm});
            skArc(sketch, "E40.5.1", {"start": v(7.57, 5.74) * mm, "mid": v(8.34, 4.55) * mm, "end": v(8.93, 3.25) * mm});
            skPoint(sketch, "E40.5.2", {"position": v(20.19, 3.56) * mm});
            skPoint(sketch, "E40.5.3", {"position": v(9.36, 1.65) * mm});
            skPoint(sketch, "E40.5.4", {"position": v(6.72, 6.72) * mm});
            skLineSegment(sketch, "E40.5.5", {"start": v(11.15, 1.97) * mm, "end": v(18.11, 3.2) * mm});
            skArc(sketch, "E40.5.6", {"start": v(8.93, 3.25) * mm, "mid": v(9.8, 2.2) * mm, "end": v(11.15, 1.97) * mm});
            skArc(sketch, "E40.5.7", {"start": v(18.11, 3.2) * mm, "mid": v(19.46, 4.1) * mm, "end": v(19.69, 5.72) * mm});
            skArc(sketch, "E40.5.8", {"start": v(7.7, 7.7) * mm, "mid": v(7.27, 6.75) * mm, "end": v(7.57, 5.74) * mm});
            skArc(sketch, "E40.5.9", {"start": v(15.98, 12.84) * mm, "mid": v(14.53, 13.59) * mm, "end": v(13, 13) * mm});
            skArc(sketch, "E40.5.10", {"start": v(15.98, 12.84) * mm, "mid": v(18.18, 9.47) * mm, "end": v(19.69, 5.72) * mm});
            skLineSegment(sketch, "E41.1.6.0", {"start": v(0, 18.4) * mm, "end": v(0, 10.9) * mm});
            skArc(sketch, "E41.3.6.0", {"start": v(1.3, 9.41) * mm, "mid": v(2.68, 9.11) * mm, "end": v(4.01, 8.61) * mm});
            skPoint(sketch, "E41.7.6.0", {"position": v(11.76, 16.8) * mm});
            skPoint(sketch, "E41.8.6.0", {"position": v(5.45, 7.78) * mm});
            skPoint(sketch, "E41.9.6.0", {"position": v(0, 9.5) * mm});
            skLineSegment(sketch, "E41.10.6.0", {"start": v(6.5, 9.28) * mm, "end": v(10.55, 15.07) * mm});
            skArc(sketch, "E41.13.6.0", {"start": v(4.01, 8.61) * mm, "mid": v(5.38, 8.5) * mm, "end": v(6.5, 9.28) * mm});
            skArc(sketch, "E41.17.6.0", {"start": v(10.55, 15.07) * mm, "mid": v(10.86, 16.67) * mm, "end": v(9.87, 17.97) * mm});
            skArc(sketch, "E41.21.6.0", {"start": v(0, 10.9) * mm, "mid": v(0.37, 9.91) * mm, "end": v(1.3, 9.41) * mm});
            skArc(sketch, "E41.25.6.0", {"start": v(2.22, 20.38) * mm, "mid": v(0.66, 19.88) * mm, "end": v(0, 18.4) * mm});
            skArc(sketch, "E41.29.6.0", {"start": v(2.22, 20.38) * mm, "mid": v(6.16, 19.55) * mm, "end": v(9.87, 17.97) * mm});
            skLineSegment(sketch, "E41.1.7.0", {"start": v(-13, 13) * mm, "end": v(-7.7, 7.7) * mm});
            skArc(sketch, "E41.3.7.0", {"start": v(-5.74, 7.57) * mm, "mid": v(-4.55, 8.34) * mm, "end": v(-3.25, 8.93) * mm});
            skPoint(sketch, "E41.7.7.0", {"position": v(-3.56, 20.19) * mm});
            skPoint(sketch, "E41.8.7.0", {"position": v(-1.65, 9.36) * mm});
            skPoint(sketch, "E41.9.7.0", {"position": v(-6.72, 6.72) * mm});
            skLineSegment(sketch, "E41.10.7.0", {"start": v(-1.97, 11.15) * mm, "end": v(-3.2, 18.11) * mm});
            skArc(sketch, "E41.13.7.0", {"start": v(-3.25, 8.93) * mm, "mid": v(-2.2, 9.8) * mm, "end": v(-1.97, 11.15) * mm});
            skArc(sketch, "E41.17.7.0", {"start": v(-3.2, 18.11) * mm, "mid": v(-4.1, 19.46) * mm, "end": v(-5.72, 19.69) * mm});
            skArc(sketch, "E41.21.7.0", {"start": v(-7.7, 7.7) * mm, "mid": v(-6.75, 7.27) * mm, "end": v(-5.74, 7.57) * mm});
            skArc(sketch, "E41.25.7.0", {"start": v(-12.84, 15.98) * mm, "mid": v(-13.59, 14.53) * mm, "end": v(-13, 13) * mm});
            skArc(sketch, "E41.29.7.0", {"start": v(-12.84, 15.98) * mm, "mid": v(-9.47, 18.18) * mm, "end": v(-5.72, 19.69) * mm});
            skSolve(sketch);
        }
        {
            var Q0;
            Q0 = qSketchRegion(id + "F4", true);
            extrude(context, id + "F5", {"entities" : qUnion([Q0]), "operationType" : NewBodyOperationType.REMOVE, "endBound" : BoundingType.UP_TO_NEXT, "oppositeDirection" : true, "depth" : 25 * mm, "offsetDistance" : 25 * mm});
        }
        {
            var Q0;
            {var subQ0=sQuery(id+"F0.wireOp",EDGE,"E1");Q0=makeQuery(id+"F3.boolean.opBoolean","SPLIT",FACE,{"disambiguationData":[TD([makeQuery(id+"F1.opExtrude","SWEPT_FACE",FACE,{"disambiguationData":[OSD([subQ0])]})])],"derivedFrom":makeQuery(id+"F1.opExtrude","CAP_FACE",FACE,{"disambiguationData":[OSD([sQuery(id+"F0.wireOp",EDGE,"E0"),subQ0])],"isStart":false})});}
            var sketch = newSketch(context, id + "F6", { "sketchPlane" : qUnion([Q0])});
            skCircle(sketch, "E42.0", {"center": v(0, 0) * mm, "radius": 8 * mm});
            skCircle(sketch, "E43.0", {"center": v(0, 0) * mm, "radius": 6.5 * mm});
            skSolve(sketch);
        }
        {
            var Q0;
            Q0 = qSketchRegion(id + "F6", true);
            extrude(context, id + "F7", {"entities" : qUnion([Q0]), "operationType" : NewBodyOperationType.ADD, "depth" : 7 * mm, "offsetDistance" : 25 * mm});
        }
        {
            var Q0;
            {var subQ0=sQuery(id+"F0.wireOp",EDGE,"E1");Q0=makeQuery(id+"F3.boolean.opBoolean","SPLIT",FACE,{"disambiguationData":[TD([makeQuery(id+"F1.opExtrude","SWEPT_FACE",FACE,{"disambiguationData":[OSD([subQ0])]})])],"derivedFrom":makeQuery(id+"F1.opExtrude","CAP_FACE",FACE,{"disambiguationData":[OSD([sQuery(id+"F0.wireOp",EDGE,"E0"),subQ0])],"isStart":false})});}
            var sketch = newSketch(context, id + "F8", { "sketchPlane" : qUnion([Q0])});
            skLineSegment(sketch, "E44", {"start": v(-22.47, 6.87) * mm, "end": v(-20.56, 6.29) * mm});
            skLineSegment(sketch, "E45", {"start": v(-20.35, 11.75) * mm, "end": v(-18.62, 10.75) * mm});
            skArc(sketch, "E46", {"start": v(-20.56, 6.29) * mm, "mid": v(-19.72, 8.57) * mm, "end": v(-18.62, 10.75) * mm});
            skArc(sketch, "E47", {"start": v(-22.47, 6.87) * mm, "mid": v(-21.55, 9.37) * mm, "end": v(-20.35, 11.75) * mm});
            skArc(sketch, "E48.1.0", {"start": v(-22.9, -5.29) * mm, "mid": v(-23.35, -2.66) * mm, "end": v(-23.5, 0) * mm});
            skArc(sketch, "E48.1.1", {"start": v(-20.95, -4.84) * mm, "mid": v(-21.36, -2.43) * mm, "end": v(-21.5, 0) * mm});
            skLineSegment(sketch, "E48.1.2", {"start": v(-23.5, 0) * mm, "end": v(-21.5, 0) * mm});
            skLineSegment(sketch, "E48.1.3", {"start": v(-22.9, -5.29) * mm, "end": v(-20.95, -4.84) * mm});
            skArc(sketch, "E48.2.0", {"start": v(-17.19, -16.03) * mm, "mid": v(-18.9, -13.98) * mm, "end": v(-20.35, -11.75) * mm});
            skArc(sketch, "E48.2.1", {"start": v(-15.72, -14.66) * mm, "mid": v(-17.28, -12.79) * mm, "end": v(-18.62, -10.75) * mm});
            skLineSegment(sketch, "E48.2.2", {"start": v(-20.35, -11.75) * mm, "end": v(-18.62, -10.75) * mm});
            skLineSegment(sketch, "E48.2.3", {"start": v(-17.19, -16.03) * mm, "end": v(-15.72, -14.66) * mm});
            skArc(sketch, "E48.3.0", {"start": v(-6.87, -22.47) * mm, "mid": v(-9.37, -21.55) * mm, "end": v(-11.75, -20.35) * mm});
            skArc(sketch, "E48.3.1", {"start": v(-6.29, -20.56) * mm, "mid": v(-8.57, -19.72) * mm, "end": v(-10.75, -18.62) * mm});
            skLineSegment(sketch, "E48.3.2", {"start": v(-11.75, -20.35) * mm, "end": v(-10.75, -18.62) * mm});
            skLineSegment(sketch, "E48.3.3", {"start": v(-6.87, -22.47) * mm, "end": v(-6.29, -20.56) * mm});
            skArc(sketch, "E48.4.0", {"start": v(5.29, -22.9) * mm, "mid": v(2.66, -23.35) * mm, "end": v(0, -23.5) * mm});
            skArc(sketch, "E48.4.1", {"start": v(4.84, -20.95) * mm, "mid": v(2.43, -21.36) * mm, "end": v(0, -21.5) * mm});
            skLineSegment(sketch, "E48.4.2", {"start": v(0, -23.5) * mm, "end": v(0, -21.5) * mm});
            skLineSegment(sketch, "E48.4.3", {"start": v(5.29, -22.9) * mm, "end": v(4.84, -20.95) * mm});
            skArc(sketch, "E48.5.0", {"start": v(16.03, -17.19) * mm, "mid": v(13.98, -18.9) * mm, "end": v(11.75, -20.35) * mm});
            skArc(sketch, "E48.5.1", {"start": v(14.66, -15.72) * mm, "mid": v(12.79, -17.28) * mm, "end": v(10.75, -18.62) * mm});
            skLineSegment(sketch, "E48.5.2", {"start": v(11.75, -20.35) * mm, "end": v(10.75, -18.62) * mm});
            skLineSegment(sketch, "E48.5.3", {"start": v(16.03, -17.19) * mm, "end": v(14.66, -15.72) * mm});
            skArc(sketch, "E48.6.0", {"start": v(22.47, -6.87) * mm, "mid": v(21.55, -9.37) * mm, "end": v(20.35, -11.75) * mm});
            skArc(sketch, "E48.6.1", {"start": v(20.56, -6.29) * mm, "mid": v(19.72, -8.57) * mm, "end": v(18.62, -10.75) * mm});
            skLineSegment(sketch, "E48.6.2", {"start": v(20.35, -11.75) * mm, "end": v(18.62, -10.75) * mm});
            skLineSegment(sketch, "E48.6.3", {"start": v(22.47, -6.87) * mm, "end": v(20.56, -6.29) * mm});
            skArc(sketch, "E48.7.0", {"start": v(22.9, 5.29) * mm, "mid": v(23.35, 2.66) * mm, "end": v(23.5, 0) * mm});
            skArc(sketch, "E48.7.1", {"start": v(20.95, 4.84) * mm, "mid": v(21.36, 2.43) * mm, "end": v(21.5, 0) * mm});
            skLineSegment(sketch, "E48.7.2", {"start": v(23.5, 0) * mm, "end": v(21.5, 0) * mm});
            skLineSegment(sketch, "E48.7.3", {"start": v(22.9, 5.29) * mm, "end": v(20.95, 4.84) * mm});
            skArc(sketch, "E48.8.0", {"start": v(17.19, 16.03) * mm, "mid": v(18.9, 13.98) * mm, "end": v(20.35, 11.75) * mm});
            skArc(sketch, "E48.8.1", {"start": v(15.72, 14.66) * mm, "mid": v(17.28, 12.79) * mm, "end": v(18.62, 10.75) * mm});
            skLineSegment(sketch, "E48.8.2", {"start": v(20.35, 11.75) * mm, "end": v(18.62, 10.75) * mm});
            skLineSegment(sketch, "E48.8.3", {"start": v(17.19, 16.03) * mm, "end": v(15.72, 14.66) * mm});
            skArc(sketch, "E48.9.0", {"start": v(6.87, 22.47) * mm, "mid": v(9.37, 21.55) * mm, "end": v(11.75, 20.35) * mm});
            skArc(sketch, "E48.9.1", {"start": v(6.29, 20.56) * mm, "mid": v(8.57, 19.72) * mm, "end": v(10.75, 18.62) * mm});
            skLineSegment(sketch, "E48.9.2", {"start": v(11.75, 20.35) * mm, "end": v(10.75, 18.62) * mm});
            skLineSegment(sketch, "E48.9.3", {"start": v(6.87, 22.47) * mm, "end": v(6.29, 20.56) * mm});
            skArc(sketch, "E48.10.0", {"start": v(-5.29, 22.9) * mm, "mid": v(-2.66, 23.35) * mm, "end": v(0, 23.5) * mm});
            skArc(sketch, "E48.10.1", {"start": v(-4.84, 20.95) * mm, "mid": v(-2.43, 21.36) * mm, "end": v(0, 21.5) * mm});
            skLineSegment(sketch, "E48.10.2", {"start": v(0, 23.5) * mm, "end": v(0, 21.5) * mm});
            skLineSegment(sketch, "E48.10.3", {"start": v(-5.29, 22.9) * mm, "end": v(-4.84, 20.95) * mm});
            skArc(sketch, "E48.11.0", {"start": v(-16.03, 17.19) * mm, "mid": v(-13.98, 18.9) * mm, "end": v(-11.75, 20.35) * mm});
            skArc(sketch, "E48.11.1", {"start": v(-14.66, 15.72) * mm, "mid": v(-12.79, 17.28) * mm, "end": v(-10.75, 18.62) * mm});
            skLineSegment(sketch, "E48.11.2", {"start": v(-11.75, 20.35) * mm, "end": v(-10.75, 18.62) * mm});
            skLineSegment(sketch, "E48.11.3", {"start": v(-16.03, 17.19) * mm, "end": v(-14.66, 15.72) * mm});
            skSolve(sketch);
        }
        {
            var Q0;
            Q0 = qSketchRegion(id + "F8", true);
            extrude(context, id + "F9", {"entities" : qUnion([Q0]), "operationType" : NewBodyOperationType.ADD, "depth" : 7 * mm, "offsetDistance" : 25 * mm});
        }
        {
            var Q0;
            Q0=makeQuery(id+"F3.opExtrude","CAP_FACE",FACE,{"disambiguationData":[OSD([sQuery(id+"F2.wireOp",EDGE,"E2"),sQuery(id+"F2.wireOp",EDGE,"E3.0")])],"isStart":false});
            var sketch = newSketch(context, id + "F10", { "sketchPlane" : qUnion([Q0])});
            skLineSegment(sketch, "E49", {"start": v(-25.86, 2.72) * mm, "end": v(-22.87, 2.4) * mm});
            skLineSegment(sketch, "E50", {"start": v(-22.87, 2.4) * mm, "end": v(-22.7, 4) * mm});
            skLineSegment(sketch, "E51", {"start": v(-22.7, 4) * mm, "end": v(-25.66, 4.52) * mm});
            skLineSegment(sketch, "E52", {"start": v(-25.66, 4.52) * mm, "end": v(-25.86, 2.72) * mm});
            skSolve(sketch);
        }
        {
            var Q0;
            Q0 = qSketchRegion(id + "F10", true);
            var Q1;
            {var subQ0=sQuery(id+"F0.wireOp",EDGE,"E0");Q1=makeQuery(id+"F3.boolean.opBoolean","SPLIT",FACE,{"disambiguationData":[TD([makeQuery(id+"F1.opExtrude","SWEPT_FACE",FACE,{"disambiguationData":[OSD([subQ0])]})])],"derivedFrom":makeQuery(id+"F1.opExtrude","CAP_FACE",FACE,{"disambiguationData":[OSD([subQ0,sQuery(id+"F0.wireOp",EDGE,"E1")])],"isStart":false})});}
            extrude(context, id + "F11", {"entities" : qUnion([Q0]), "operationType" : NewBodyOperationType.REMOVE, "endBound" : BoundingType.UP_TO_SURFACE, "oppositeDirection" : true, "depth" : 25 * mm, "endBoundEntityFace" : qUnion([Q1]), "offsetDistance" : 25 * mm});
        }
        {
            var Q0;
            Q0=makeQuery(id+"F9.opExtrude","CAP_EDGE",EDGE,{"disambiguationData":[OSD([sQuery(id+"F8.wireOp",EDGE,"E48.1.2")])],"isStart":false});
            var Q1;
            Q1=makeQuery(id+"F9.opExtrude","CAP_EDGE",EDGE,{"disambiguationData":[OSD([sQuery(id+"F8.wireOp",EDGE,"E48.1.3")])],"isStart":false});
            var Q2;
            Q2=makeQuery(id+"F9.opExtrude","CAP_EDGE",EDGE,{"disambiguationData":[OSD([sQuery(id+"F8.wireOp",EDGE,"E48.2.2")])],"isStart":false});
            var Q3;
            Q3=makeQuery(id+"F9.opExtrude","CAP_EDGE",EDGE,{"disambiguationData":[OSD([sQuery(id+"F8.wireOp",EDGE,"E48.3.2")])],"isStart":false});
            var Q4;
            Q4=makeQuery(id+"F9.opExtrude","CAP_EDGE",EDGE,{"disambiguationData":[OSD([sQuery(id+"F8.wireOp",EDGE,"E48.2.3")])],"isStart":false});
            var Q5;
            Q5=makeQuery(id+"F9.opExtrude","CAP_EDGE",EDGE,{"disambiguationData":[OSD([sQuery(id+"F8.wireOp",EDGE,"E48.3.3")])],"isStart":false});
            var Q6;
            Q6=makeQuery(id+"F9.opExtrude","CAP_EDGE",EDGE,{"disambiguationData":[OSD([sQuery(id+"F8.wireOp",EDGE,"E48.4.2")])],"isStart":false});
            var Q7;
            Q7=makeQuery(id+"F9.opExtrude","CAP_EDGE",EDGE,{"disambiguationData":[OSD([sQuery(id+"F8.wireOp",EDGE,"E48.4.3")])],"isStart":false});
            var Q8;
            Q8=makeQuery(id+"F9.opExtrude","CAP_EDGE",EDGE,{"disambiguationData":[OSD([sQuery(id+"F8.wireOp",EDGE,"E48.5.2")])],"isStart":false});
            var Q9;
            Q9=makeQuery(id+"F9.opExtrude","CAP_EDGE",EDGE,{"disambiguationData":[OSD([sQuery(id+"F8.wireOp",EDGE,"E48.5.3")])],"isStart":false});
            var Q10;
            Q10=makeQuery(id+"F9.opExtrude","CAP_EDGE",EDGE,{"disambiguationData":[OSD([sQuery(id+"F8.wireOp",EDGE,"E48.6.2")])],"isStart":false});
            var Q11;
            Q11=makeQuery(id+"F9.opExtrude","CAP_EDGE",EDGE,{"disambiguationData":[OSD([sQuery(id+"F8.wireOp",EDGE,"E48.6.3")])],"isStart":false});
            var Q12;
            Q12=makeQuery(id+"F9.opExtrude","CAP_EDGE",EDGE,{"disambiguationData":[OSD([sQuery(id+"F8.wireOp",EDGE,"E44")])],"isStart":false});
            var Q13;
            Q13=makeQuery(id+"F9.opExtrude","CAP_EDGE",EDGE,{"disambiguationData":[OSD([sQuery(id+"F8.wireOp",EDGE,"E45")])],"isStart":false});
            var Q14;
            Q14=makeQuery(id+"F9.opExtrude","CAP_EDGE",EDGE,{"disambiguationData":[OSD([sQuery(id+"F8.wireOp",EDGE,"E48.11.3")])],"isStart":false});
            var Q15;
            Q15=makeQuery(id+"F9.opExtrude","CAP_EDGE",EDGE,{"disambiguationData":[OSD([sQuery(id+"F8.wireOp",EDGE,"E48.11.2")])],"isStart":false});
            var Q16;
            Q16=makeQuery(id+"F9.opExtrude","CAP_EDGE",EDGE,{"disambiguationData":[OSD([sQuery(id+"F8.wireOp",EDGE,"E48.10.3")])],"isStart":false});
            var Q17;
            Q17=makeQuery(id+"F9.opExtrude","CAP_EDGE",EDGE,{"disambiguationData":[OSD([sQuery(id+"F8.wireOp",EDGE,"E48.10.2")])],"isStart":false});
            var Q18;
            Q18=makeQuery(id+"F9.opExtrude","CAP_EDGE",EDGE,{"disambiguationData":[OSD([sQuery(id+"F8.wireOp",EDGE,"E48.9.3")])],"isStart":false});
            var Q19;
            Q19=makeQuery(id+"F9.opExtrude","CAP_EDGE",EDGE,{"disambiguationData":[OSD([sQuery(id+"F8.wireOp",EDGE,"E48.9.2")])],"isStart":false});
            var Q20;
            Q20=makeQuery(id+"F9.opExtrude","CAP_EDGE",EDGE,{"disambiguationData":[OSD([sQuery(id+"F8.wireOp",EDGE,"E48.8.3")])],"isStart":false});
            var Q21;
            Q21=makeQuery(id+"F9.opExtrude","CAP_EDGE",EDGE,{"disambiguationData":[OSD([sQuery(id+"F8.wireOp",EDGE,"E48.8.2")])],"isStart":false});
            var Q22;
            Q22=makeQuery(id+"F9.opExtrude","CAP_EDGE",EDGE,{"disambiguationData":[OSD([sQuery(id+"F8.wireOp",EDGE,"E48.7.3")])],"isStart":false});
            var Q23;
            Q23=makeQuery(id+"F9.opExtrude","CAP_EDGE",EDGE,{"disambiguationData":[OSD([sQuery(id+"F8.wireOp",EDGE,"E48.7.2")])],"isStart":false});
            chamfer(context, id + "F12", {"entities" : qUnion([Q0, Q1, Q2, Q3, Q4, Q5, Q6, Q7, Q8, Q9, Q10, Q11, Q12, Q13, Q14, Q15, Q16, Q17, Q18, Q19, Q20, Q21, Q22, Q23]), "width" : 1 * mm, "tangentPropagation" : true});
        }
    });
